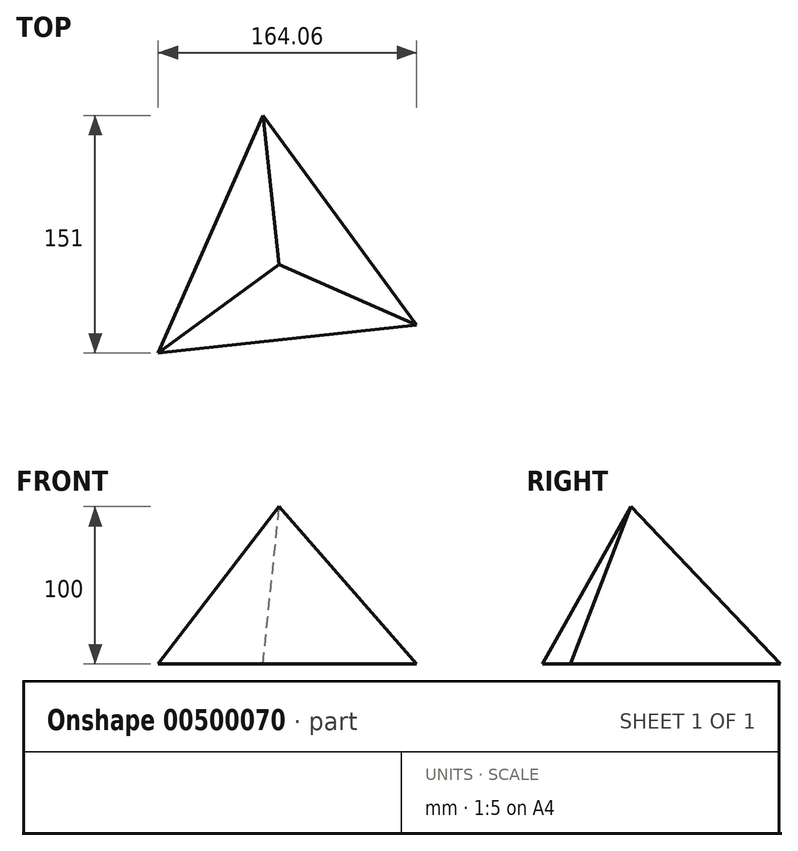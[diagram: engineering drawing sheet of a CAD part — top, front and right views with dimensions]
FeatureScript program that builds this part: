
annotation { "Feature Type Name" : "Feature", "Feature Type Description" : "" }
export const myFeature = defineFeature(function(context is Context, id is Id, definition is map)
    precondition{}
    {
        {
            var Q0;
            Q0=qCreatedBy(makeId("Top.planeOp"),FACE);
            var sketch = newSketch(context, id + "F0", { "sketchPlane" : qUnion([Q0])});
            skCircle(sketch, "E0.cCircle", {"center": v(0, 0) * mm, "radius": 95.28 * mm, "construction": true});
            skLineSegment(sketch, "E0.0", {"start": v(87.18, -38.44) * mm, "end": v(-76.88, -56.28) * mm});
            skLineSegment(sketch, "E0.1", {"start": v(-76.88, -56.28) * mm, "end": v(-10.3, 94.72) * mm});
            skLineSegment(sketch, "E0.2", {"start": v(-10.3, 94.72) * mm, "end": v(87.18, -38.44) * mm});
            skSolve(sketch);
        }
        {
            var Q0;
            Q0=qCreatedBy(makeId("Top.planeOp"),FACE);
            cPlane(context, id + "F1", {"entities" : qUnion([Q0]), "cplaneType" : CPlaneType.OFFSET, "offset" : 100 * mm, "width" : 152.4 * mm, "height" : 152.4 * mm});
        }
        {
            var Q0;
            Q0=qCreatedBy(id+"F1.planeOp",FACE);
            var sketch = newSketch(context, id + "F2", { "sketchPlane" : qUnion([Q0])});
            skPoint(sketch, "E1", {"position": v(0, 0) * mm});
            skSolve(sketch);
        }
        {
            var Q0;
            Q0=makeQuery(id+"F0.imprint","IMPRINT",FACE,{"disambiguationData":[TD([[makeQuery(id+"F0.imprint","IMPRINT",EDGE,{"derivedFrom":sQuery(id+"F0.wireOp",EDGE,"E0.0")}),-1.0]])]});
            var Q1;
            Q1=sQuery(id+"F2.wireOp",VERTEX,"E1");
            loft(context, id + "F3", {"sheetProfilesArray" : [{ "sheetProfileEntities" : qUnion([Q0]) }, { "sheetProfileEntities" : qUnion([Q1]) }]});
        }
    });
